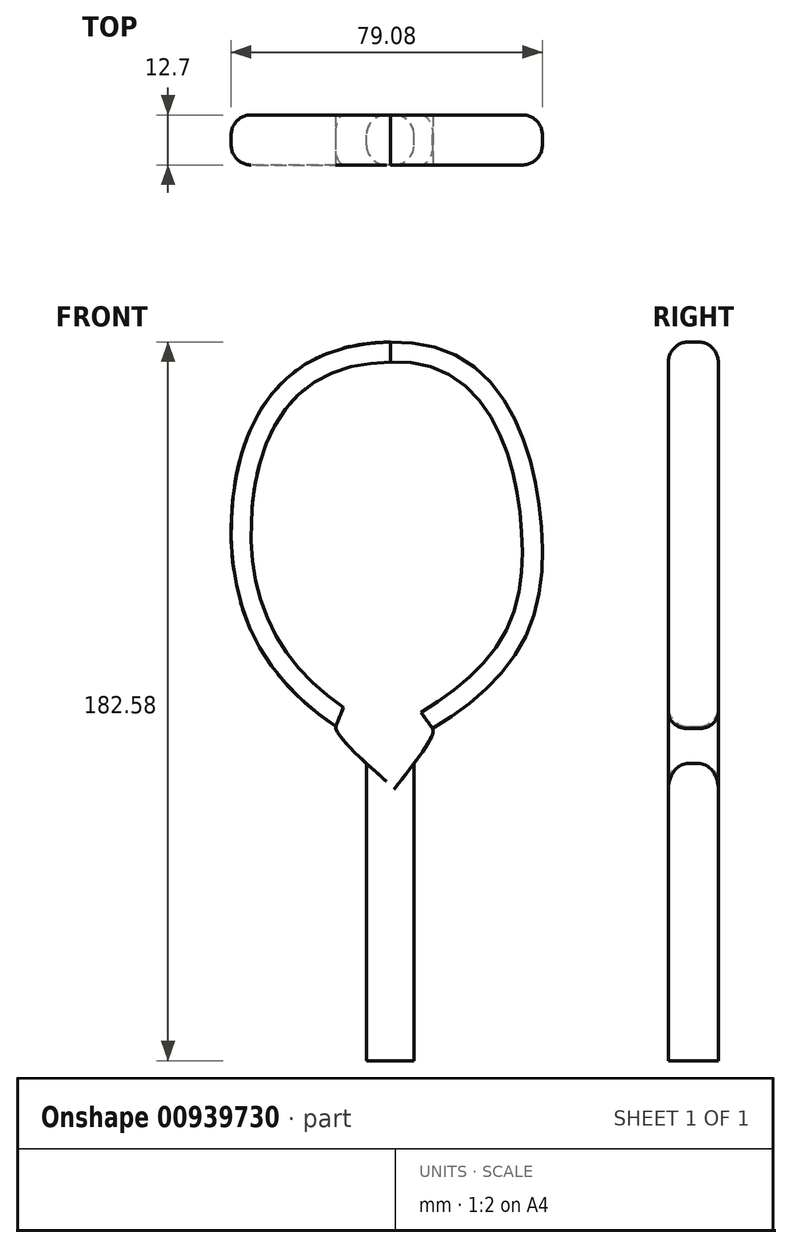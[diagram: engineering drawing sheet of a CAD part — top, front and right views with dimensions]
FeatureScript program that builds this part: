
annotation { "Feature Type Name" : "Feature", "Feature Type Description" : "" }
export const myFeature = defineFeature(function(context is Context, id is Id, definition is map)
    precondition{}
    {
        {
            var Q0;
            Q0=qCreatedBy(makeId("Front.planeOp"),FACE);
            var sketch = newSketch(context, id + "F0", { "sketchPlane" : qUnion([Q0])});
            skLineSegment(sketch, "E0.bottom", {"start": v(0, 0) * mm, "end": v(-12.1, 0) * mm});
            skLineSegment(sketch, "E0.top", {"start": v(0, -75.51) * mm, "end": v(-12.1, -75.51) * mm});
            skLineSegment(sketch, "E0.left", {"start": v(0, 0) * mm, "end": v(0, -75.51) * mm});
            skLineSegment(sketch, "E0.right", {"start": v(-12.1, 0) * mm, "end": v(-12.1, -75.51) * mm});
            skPoint(sketch, "E1.2.internal.snap0", {"position": v(-6.05, 0) * mm});
            skFitSpline(sketch, "E1", {"points": [v(-12.1, 0) * mm, v(-19.88, 9.4) * mm, v(-6.05, 7.74) * mm, v(4.74, 8.85) * mm, v(0, 0) * mm], "startDerivative": vector(-36.17, 32.51) * mm, "endDerivative": vector(-35.79, -46.54) * mm});
            skFitSpline(sketch, "E2", {"points": [v(-19.88, 9.4) * mm, v(-46.43, 61.4) * mm, v(-6.05, 107.04) * mm], "startDerivative": vector(-120.78, 80.52) * mm, "endDerivative": vector(182.13, 1.64) * mm});
            skFitSpline(sketch, "E3", {"points": [v(-6.05, 107.04) * mm, v(32.4, 59.2) * mm, v(4.74, 8.85) * mm], "startDerivative": vector(168.26, 6.53) * mm, "endDerivative": vector(-145.13, -87.75) * mm});
            skSolve(sketch);
        }
        {
            var Q0;
            Q0 = qSketchRegion(id + "F0", true);
            extrude(context, id + "F1", {"entities" : qUnion([Q0]), "depth" : 12.7 * mm, "offsetDistance" : 25.4 * mm});
        }
        {
            var Q0;
            Q0=makeQuery(id+"F1.opExtrude","CAP_EDGE",EDGE,{"disambiguationData":[OSD([sQuery(id+"F0.wireOp",EDGE,"E3")])],"isStart":true});
            var Q1;
            Q1=makeQuery(id+"F1.opExtrude","CAP_EDGE",EDGE,{"disambiguationData":[OSD([sQuery(id+"F0.wireOp",EDGE,"E0.left")])],"isStart":true});
            fillet(context, id + "F2", {"entities" : qUnion([Q0, Q1]), "radius" : 5.08 * mm, "tangentPropagation" : true, "allowEdgeOverflow" : false});
        }
        {
            var Q0;
            Q0=makeQuery(id+"F1.opExtrude","CAP_EDGE",EDGE,{"disambiguationData":[OSD([sQuery(id+"F0.wireOp",EDGE,"E3")])],"isStart":false});
            fillet(context, id + "F3", {"entities" : qUnion([Q0]), "radius" : 5.08 * mm, "tangentPropagation" : true, "allowEdgeOverflow" : false});
        }
        {
            var Q0;
            Q0=makeQuery(id+"F1.opExtrude","CAP_EDGE",EDGE,{"disambiguationData":[OSD([sQuery(id+"F0.wireOp",EDGE,"E0.right")])],"isStart":false});
            fillet(context, id + "F4", {"entities" : qUnion([Q0]), "radius" : 5.08 * mm, "tangentPropagation" : true, "allowEdgeOverflow" : false});
        }
        {
            var Q0;
            Q0=makeQuery(id+"F1.opExtrude","CAP_EDGE",EDGE,{"disambiguationData":[OSD([sQuery(id+"F0.wireOp",EDGE,"E0.right")])],"isStart":true});
            var Q1;
            Q1=makeQuery(id+"F1.opExtrude","CAP_EDGE",EDGE,{"disambiguationData":[OSD([sQuery(id+"F0.wireOp",EDGE,"E0.left")])],"isStart":false});
            fillet(context, id + "F5", {"entities" : qUnion([Q0, Q1]), "radius" : 5.08 * mm, "tangentPropagation" : true, "allowEdgeOverflow" : false});
        }
    });
